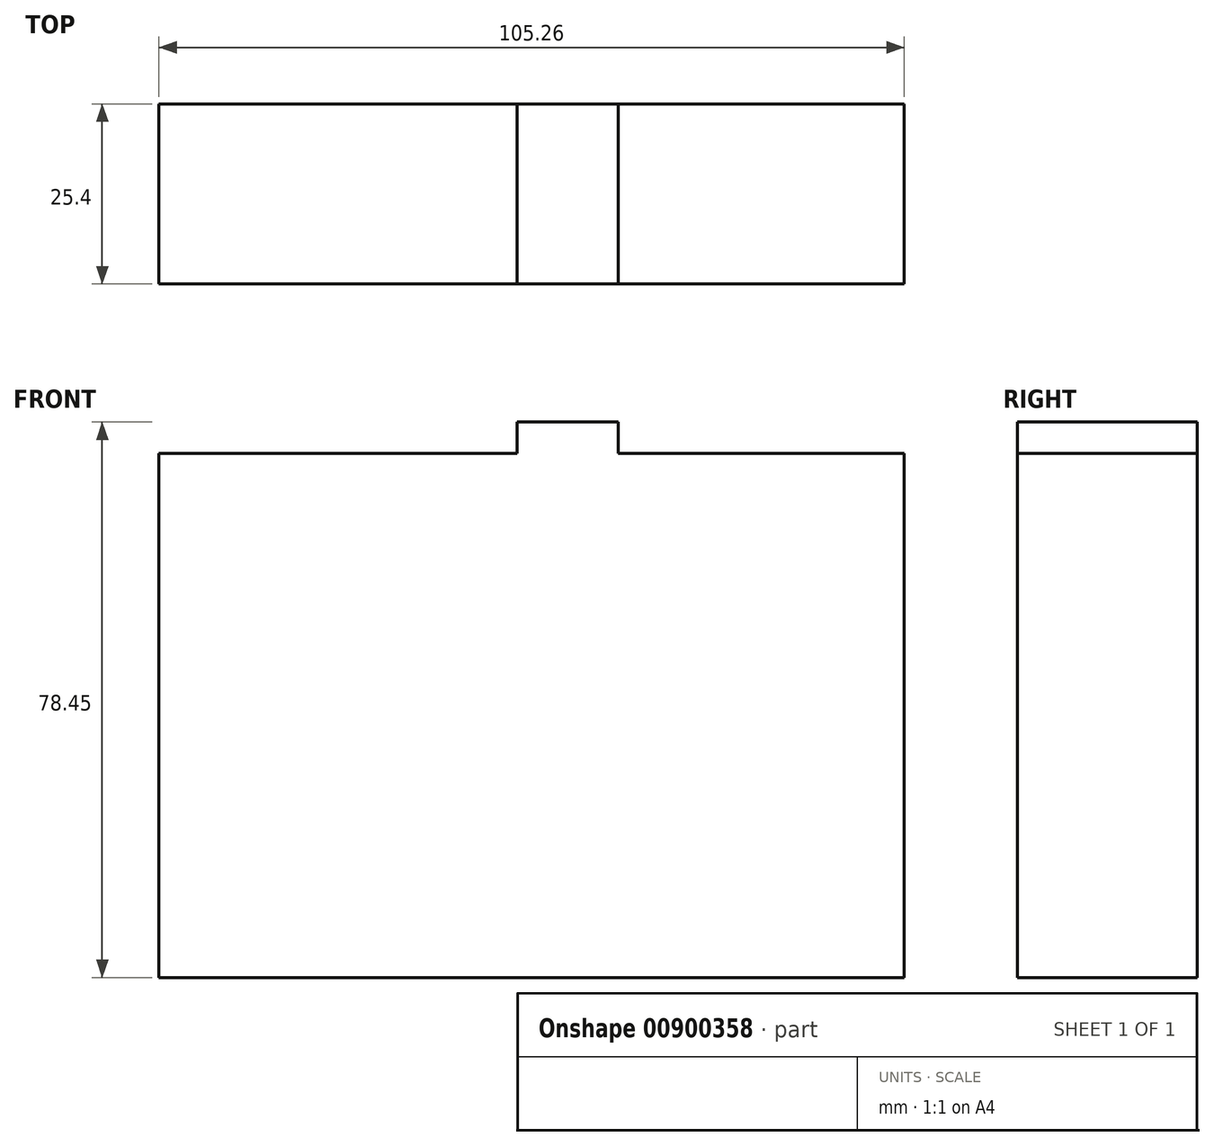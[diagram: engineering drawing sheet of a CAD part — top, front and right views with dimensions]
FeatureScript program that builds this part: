
annotation { "Feature Type Name" : "Feature", "Feature Type Description" : "" }
export const myFeature = defineFeature(function(context is Context, id is Id, definition is map)
    precondition{}
    {
        {
            var Q0;
            Q0=qCreatedBy(makeId("Front.planeOp"),FACE);
            var sketch = newSketch(context, id + "F0", { "sketchPlane" : qUnion([Q0])});
            skLineSegment(sketch, "E0.bottom", {"start": v(-50.59, 37.97) * mm, "end": v(54.67, 37.97) * mm});
            skLineSegment(sketch, "E0.top", {"start": v(-50.59, -36.02) * mm, "end": v(54.67, -36.02) * mm});
            skLineSegment(sketch, "E0.left", {"start": v(-50.59, 37.97) * mm, "end": v(-50.59, -36.02) * mm});
            skLineSegment(sketch, "E0.right", {"start": v(54.67, 37.97) * mm, "end": v(54.67, -36.02) * mm});
            skLineSegment(sketch, "E1.bottom", {"start": v(0, 42.43) * mm, "end": v(14.27, 42.43) * mm});
            skLineSegment(sketch, "E1.top", {"start": v(0, 35.64) * mm, "end": v(14.27, 35.64) * mm});
            skLineSegment(sketch, "E1.left", {"start": v(0, 42.43) * mm, "end": v(0, 35.64) * mm});
            skLineSegment(sketch, "E1.right", {"start": v(14.27, 42.43) * mm, "end": v(14.27, 35.64) * mm});
            skSolve(sketch);
        }
        {
            var Q0;
            {var subQ5=sQuery(id+"F0.wireOp",EDGE,"E1.bottom");Q0=makeQuery(id+"F0.imprint","IMPRINT",FACE,{"disambiguationData":[TD([[makeQuery(id+"F0.imprint","IMPRINT",EDGE,{"derivedFrom":subQ5}),-1.0]])]});}
            var Q1;
            {var subQ5=sQuery(id+"F0.wireOp",EDGE,"E1.top");Q1=makeQuery(id+"F0.imprint","IMPRINT",FACE,{"disambiguationData":[TD([[makeQuery(id+"F0.imprint","IMPRINT",EDGE,{"derivedFrom":subQ5}),1.0]])]});}
            var Q2;
            Q2=makeQuery(id+"F0.imprint","IMPRINT",FACE,{"disambiguationData":[TD([[makeQuery(id+"F0.imprint","IMPRINT",EDGE,{"derivedFrom":sQuery(id+"F0.wireOp",EDGE,"E0.top")}),1.0]])]});
            extrude(context, id + "F1", {"entities" : qUnion([Q0, Q1, Q2]), "depth" : 25.4 * mm, "offsetDistance" : 25.4 * mm});
        }
    });
